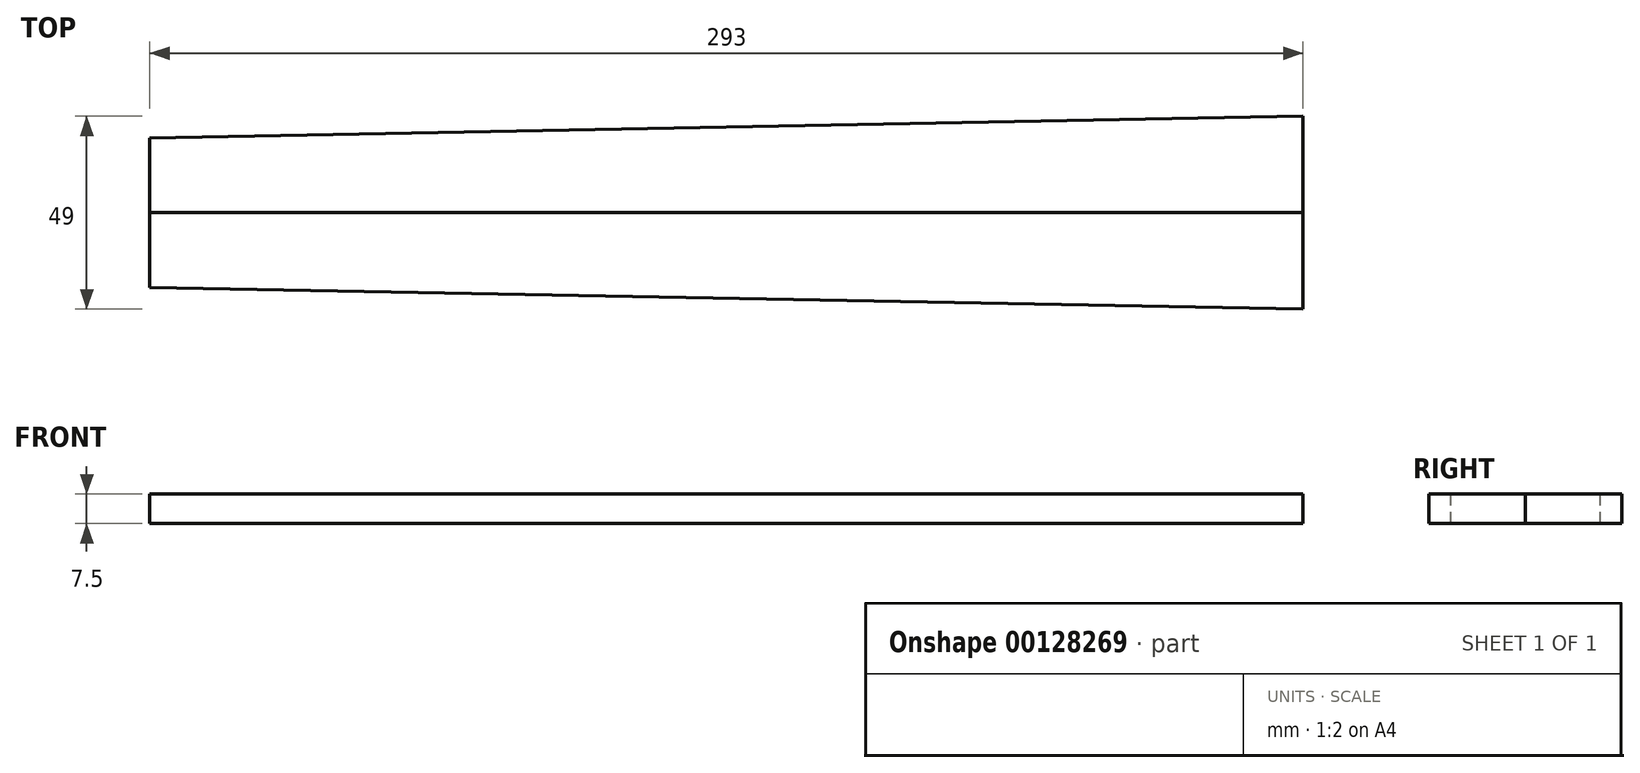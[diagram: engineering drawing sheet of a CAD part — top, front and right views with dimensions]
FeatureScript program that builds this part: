
annotation { "Feature Type Name" : "Feature", "Feature Type Description" : "" }
export const myFeature = defineFeature(function(context is Context, id is Id, definition is map)
    precondition{}
    {
        {
            var Q0;
            Q0=qCreatedBy(makeId("Top.planeOp"),FACE);
            var sketch = newSketch(context, id + "F0", { "sketchPlane" : qUnion([Q0])});
            skLineSegment(sketch, "E0", {"start": v(-293, 0) * mm, "end": v(0, 0) * mm});
            skLineSegment(sketch, "E1", {"start": v(-293, 0) * mm, "end": v(-293, -19) * mm});
            skLineSegment(sketch, "E2", {"start": v(0, -24.5) * mm, "end": v(0, 0) * mm});
            skPoint(sketch, "E3.end.orphan", {"position": v(0, -123.72) * mm});
            skLineSegment(sketch, "E4", {"start": v(-293, -19) * mm, "end": v(0, -24.5) * mm});
            skSolve(sketch);
        }
        {
            var Q0;
            Q0=makeQuery(id+"F0.imprint","IMPRINT",FACE,{"disambiguationData":[TD([[makeQuery(id+"F0.imprint","IMPRINT",EDGE,{"derivedFrom":sQuery(id+"F0.wireOp",EDGE,"E0")}),-1.0]])]});
            extrude(context, id + "F1", {"entities" : qUnion([Q0]), "oppositeDirection" : true, "depth" : 7.5 * mm});
        }
        {
            var Q0;
            Q0=makeQuery(id+"FOIHhaPpeNACnQM_1.boolean.opBoolean","SPLIT",BODY,{"disambiguationData":[OD(0.0)],"derivedFrom":makeQuery(id+"F1.opExtrude","SWEPT_BODY",BODY,{"disambiguationData":[OSD([sQuery(id+"F0.wireOp",EDGE,"E0"),sQuery(id+"F0.wireOp",EDGE,"E1"),sQuery(id+"F0.wireOp",EDGE,"E2"),sQuery(id+"F0.wireOp",EDGE,"E4")])]})});
            var Q1;
            Q1=qCreatedBy(makeId("Front.planeOp"),FACE);
            mirror(context, id + "F2", {"entities" : qUnion([Q0]), "mirrorPlane" : qUnion([Q1])});
        }
    });
